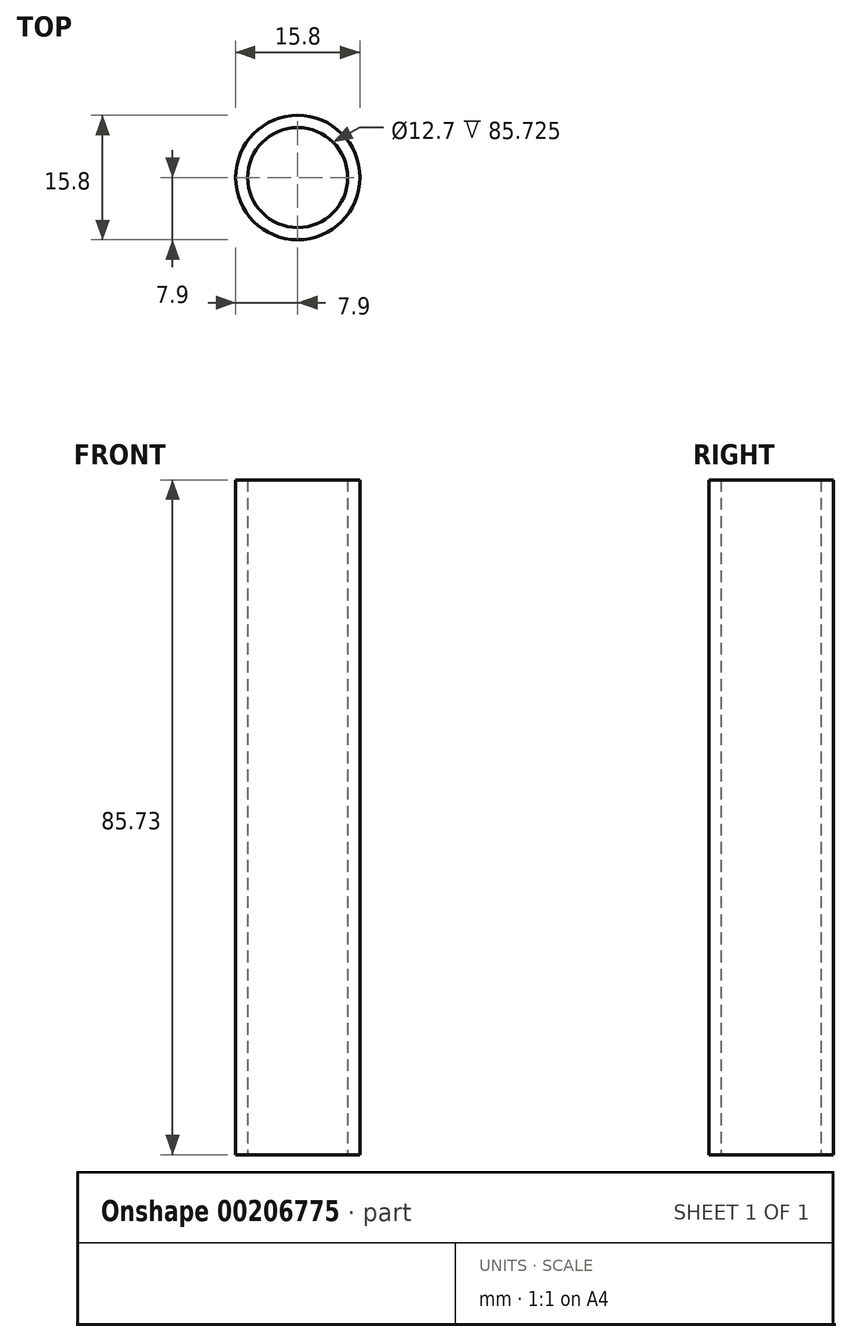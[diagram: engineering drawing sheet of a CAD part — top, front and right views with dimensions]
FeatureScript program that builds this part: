
annotation { "Feature Type Name" : "Feature", "Feature Type Description" : "" }
export const myFeature = defineFeature(function(context is Context, id is Id, definition is map)
    precondition{}
    {
        {
            var Q0;
            Q0=qCreatedBy(makeId("Top.planeOp"),FACE);
            var sketch = newSketch(context, id + "F0", { "sketchPlane" : qUnion([Q0])});
            skCircle(sketch, "E0", {"center": v(0, 0) * mm, "radius": 7.9 * mm});
            skCircle(sketch, "E1", {"center": v(0, 0) * mm, "radius": 6.35 * mm});
            skSolve(sketch);
        }
        {
            var Q0;
            Q0 = qSketchRegion(id + "F0", true);
            extrude(context, id + "F1", {"entities" : qUnion([Q0]), "depth" : 85.72 * mm});
        }
    });
